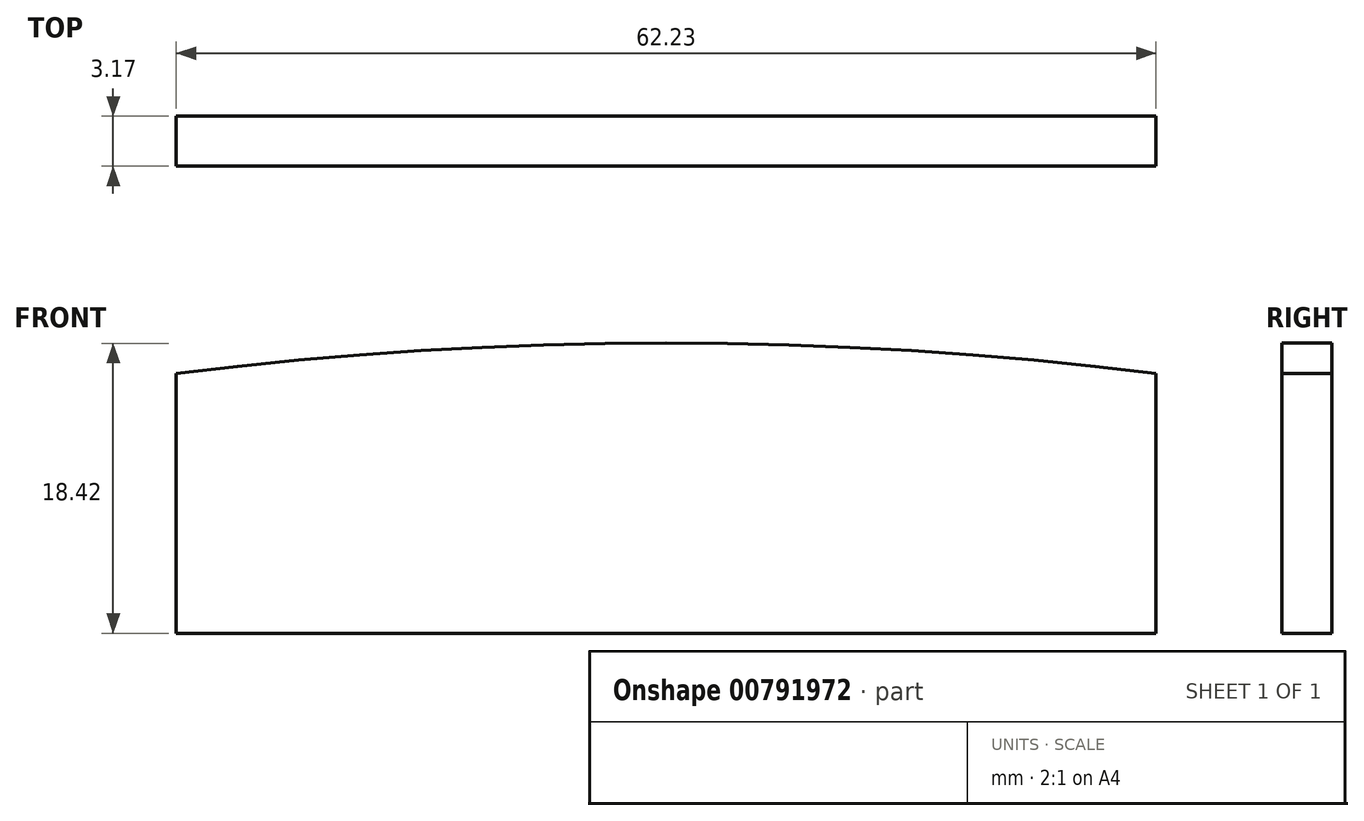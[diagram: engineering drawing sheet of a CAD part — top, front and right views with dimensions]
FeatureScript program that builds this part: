
annotation { "Feature Type Name" : "Feature", "Feature Type Description" : "" }
export const myFeature = defineFeature(function(context is Context, id is Id, definition is map)
    precondition{}
    {
        {
            var Q0;
            Q0=qCreatedBy(makeId("Front.planeOp"),FACE);
            var sketch = newSketch(context, id + "F0", { "sketchPlane" : qUnion([Q0])});
            skLineSegment(sketch, "E0.bottom", {"start": v(0, 0) * mm, "end": v(62.23, 0) * mm});
            skLineSegment(sketch, "E0.top", {"start": v(0, 16.51) * mm, "end": v(62.23, 16.51) * mm});
            skLineSegment(sketch, "E0.left", {"start": v(0, 0) * mm, "end": v(0, 16.51) * mm});
            skLineSegment(sketch, "E0.right", {"start": v(62.23, 0) * mm, "end": v(62.23, 16.51) * mm});
            skArc(sketch, "E1", {"start": v(62.23, 16.51) * mm, "mid": v(31.12, 18.42) * mm, "end": v(0, 16.51) * mm});
            skSolve(sketch);
        }
        {
            var Q0;
            Q0 = qSketchRegion(id + "F0", true);
            extrude(context, id + "F1", {"entities" : qUnion([Q0]), "depth" : 3.17 * mm, "offsetDistance" : 25.4 * mm});
        }
    });
